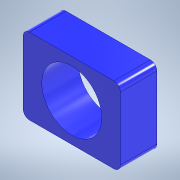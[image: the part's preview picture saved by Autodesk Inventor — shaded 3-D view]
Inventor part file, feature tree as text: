
AUTODESK INVENTOR PART (.ipt)
format: ipt  version: 2022 (Build 260153000, 153)  size: 113,664 bytes
history: native  units: in
note: dims shown in document units (in); Inventor stores cm internally (conversion verified against a paired STEP export)
features: extrude x1, fillet x1, sketch x1
ambient origin geometry x8: Origin, YZ Plane, XZ Plane, XY Plane, X Axis, Y Axis, Z Axis, Center Point
bodies: Solid1 (feature_tree)
feature tree (3):
  extrude  "Extrusion1"  Depth=0.1575in
  fillet  "Fillet1"  Radius=0.8858in
  sketch  "Sketch1"  dims[d0=1.4567in d1=0.1969in d3=0.8858in d4=0.0in d5=2.3622in d6=0.1575in]
